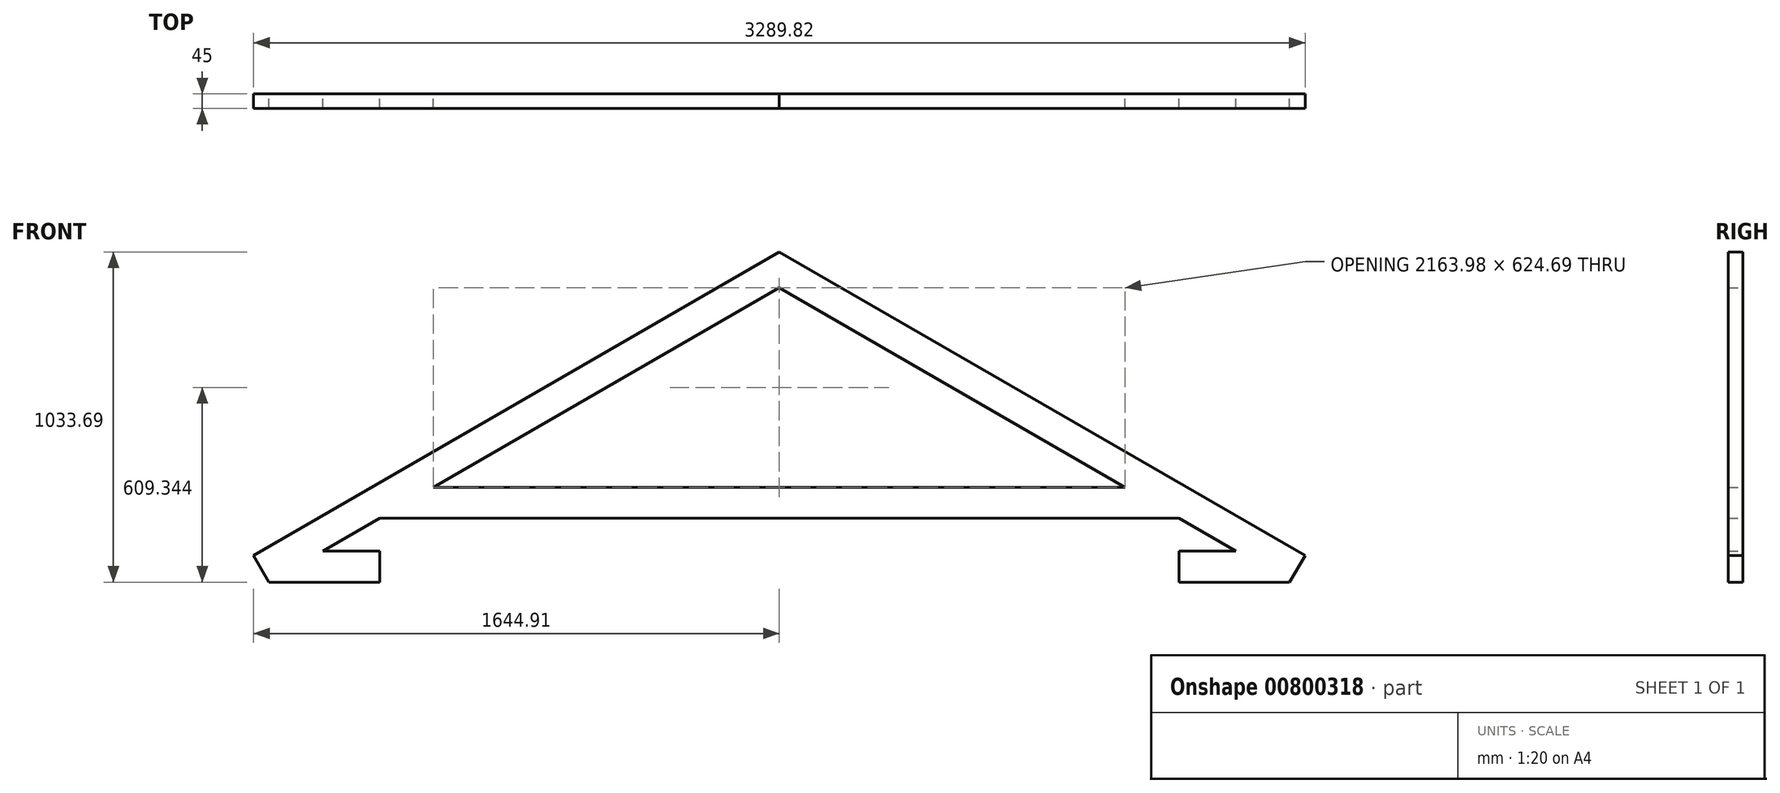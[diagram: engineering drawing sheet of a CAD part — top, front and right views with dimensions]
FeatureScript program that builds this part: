
annotation { "Feature Type Name" : "Feature", "Feature Type Description" : "" }
export const myFeature = defineFeature(function(context is Context, id is Id, definition is map)
    precondition{}
    {
        {
            var Q0;
            Q0=qCreatedBy(makeId("Front.planeOp"),FACE);
            var sketch = newSketch(context, id + "F0", { "sketchPlane" : qUnion([Q0])});
            skLineSegment(sketch, "E0", {"start": v(1644.91, -116) * mm, "end": v(0, 833.7) * mm});
            skLineSegment(sketch, "E1", {"start": v(1644.91, -116) * mm, "end": v(1596.41, -200) * mm});
            skLineSegment(sketch, "E2", {"start": v(1596.41, -200) * mm, "end": v(0, 721.69) * mm});
            skLineSegment(sketch, "E3", {"start": v(0, 721.69) * mm, "end": v(0, 833.7) * mm});
            skLineSegment(sketch, "E4", {"start": v(-1596.41, -200) * mm, "end": v(0, 721.69) * mm});
            skLineSegment(sketch, "E5", {"start": v(0, 0) * mm, "end": v(1250, 0) * mm});
            skLineSegment(sketch, "E6", {"start": v(0, 0) * mm, "end": v(-1250, 0) * mm});
            skLineSegment(sketch, "E7.bottom", {"start": v(1250, 0) * mm, "end": v(1153, 0) * mm});
            skLineSegment(sketch, "E7.top", {"start": v(1250, -200) * mm, "end": v(1153, -200) * mm});
            skLineSegment(sketch, "E7.left", {"start": v(1250, 0) * mm, "end": v(1250, -200) * mm});
            skLineSegment(sketch, "E7.right", {"start": v(1153, 0) * mm, "end": v(1153, -200) * mm});
            skLineSegment(sketch, "E8.bottom", {"start": v(-1250, 0) * mm, "end": v(-1153, 0) * mm});
            skLineSegment(sketch, "E8.top", {"start": v(-1250, -200) * mm, "end": v(-1153, -200) * mm});
            skLineSegment(sketch, "E8.left", {"start": v(-1250, 0) * mm, "end": v(-1250, -200) * mm});
            skLineSegment(sketch, "E8.right", {"start": v(-1153, 0) * mm, "end": v(-1153, -200) * mm});
            skLineSegment(sketch, "E9", {"start": v(-1082, 97) * mm, "end": v(1082, 97) * mm});
            skLineSegment(sketch, "E10", {"start": v(-1596.41, -200) * mm, "end": v(-1644.91, -116) * mm});
            skLineSegment(sketch, "E11", {"start": v(0, 833.7) * mm, "end": v(-1644.91, -116) * mm});
            skLineSegment(sketch, "E12", {"start": v(-1596.41, -200) * mm, "end": v(-1250, -200) * mm});
            skLineSegment(sketch, "E13", {"start": v(1596.41, -200) * mm, "end": v(1250, -200) * mm});
            skLineSegment(sketch, "E14", {"start": v(0, 0) * mm, "end": v(0, 1050.4) * mm});
            skLineSegment(sketch, "E15", {"start": v(1250, -103) * mm, "end": v(1428.4, -103) * mm});
            skLineSegment(sketch, "E16", {"start": v(-1250, -103) * mm, "end": v(-1428.4, -103) * mm});
            skSolve(sketch);
        }
        {
            var Q0;
            {var subQ1=sQuery(id+"F0.wireOp",EDGE,"E3");Q0=makeQuery(id+"F0.imprint","IMPRINT",FACE,{"disambiguationData":[TD([[makeQuery(id+"F0.imprint","IMPRINT",EDGE,{"derivedFrom":subQ1}),1.0]])]});}
            var Q1;
            Q1=makeQuery(id+"F0.imprint","IMPRINT",FACE,{"disambiguationData":[TD([[makeQuery(id+"F0.imprint","IMPRINT",EDGE,{"derivedFrom":sQuery(id+"F0.wireOp",EDGE,"E0")}),1.0]])]});
            var Q2;
            Q2=makeQuery(id+"F0.imprint","IMPRINT",FACE,{"disambiguationData":[TD([[makeQuery(id+"F0.imprint","IMPRINT",EDGE,{"derivedFrom":sQuery(id+"F0.wireOp",EDGE,"E5")}),1.0]])]});
            var Q3;
            {var subQ7=sQuery(id+"F0.wireOp",EDGE,"E10");Q3=makeQuery(id+"F0.imprint","IMPRINT",FACE,{"disambiguationData":[TD([[makeQuery(id+"F0.imprint","IMPRINT",EDGE,{"derivedFrom":subQ7}),-1.0]])]});}
            var Q4;
            {var subQ5=sQuery(id+"F0.wireOp",EDGE,"E6");Q4=makeQuery(id+"F0.imprint","IMPRINT",FACE,{"disambiguationData":[TD([[makeQuery(id+"F0.imprint","IMPRINT",EDGE,{"derivedFrom":subQ5}),-1.0]])]});}
            var Q5;
            {var subQ0=sQuery(id+"F0.wireOp",EDGE,"E12");Q5=makeQuery(id+"F0.imprint","IMPRINT",FACE,{"disambiguationData":[TD([[makeQuery(id+"F0.imprint","IMPRINT",EDGE,{"derivedFrom":subQ0}),1.0]])]});}
            var Q6;
            {var subQ0=sQuery(id+"F0.wireOp",EDGE,"E13");Q6=makeQuery(id+"F0.imprint","IMPRINT",FACE,{"disambiguationData":[TD([[makeQuery(id+"F0.imprint","IMPRINT",EDGE,{"derivedFrom":subQ0}),-1.0]])]});}
            extrude(context, id + "F1", {"entities" : qUnion([Q0, Q1, Q2, Q3, Q4, Q5, Q6]), "depth" : 45 * mm, "offsetDistance" : 25 * mm});
        }
    });
